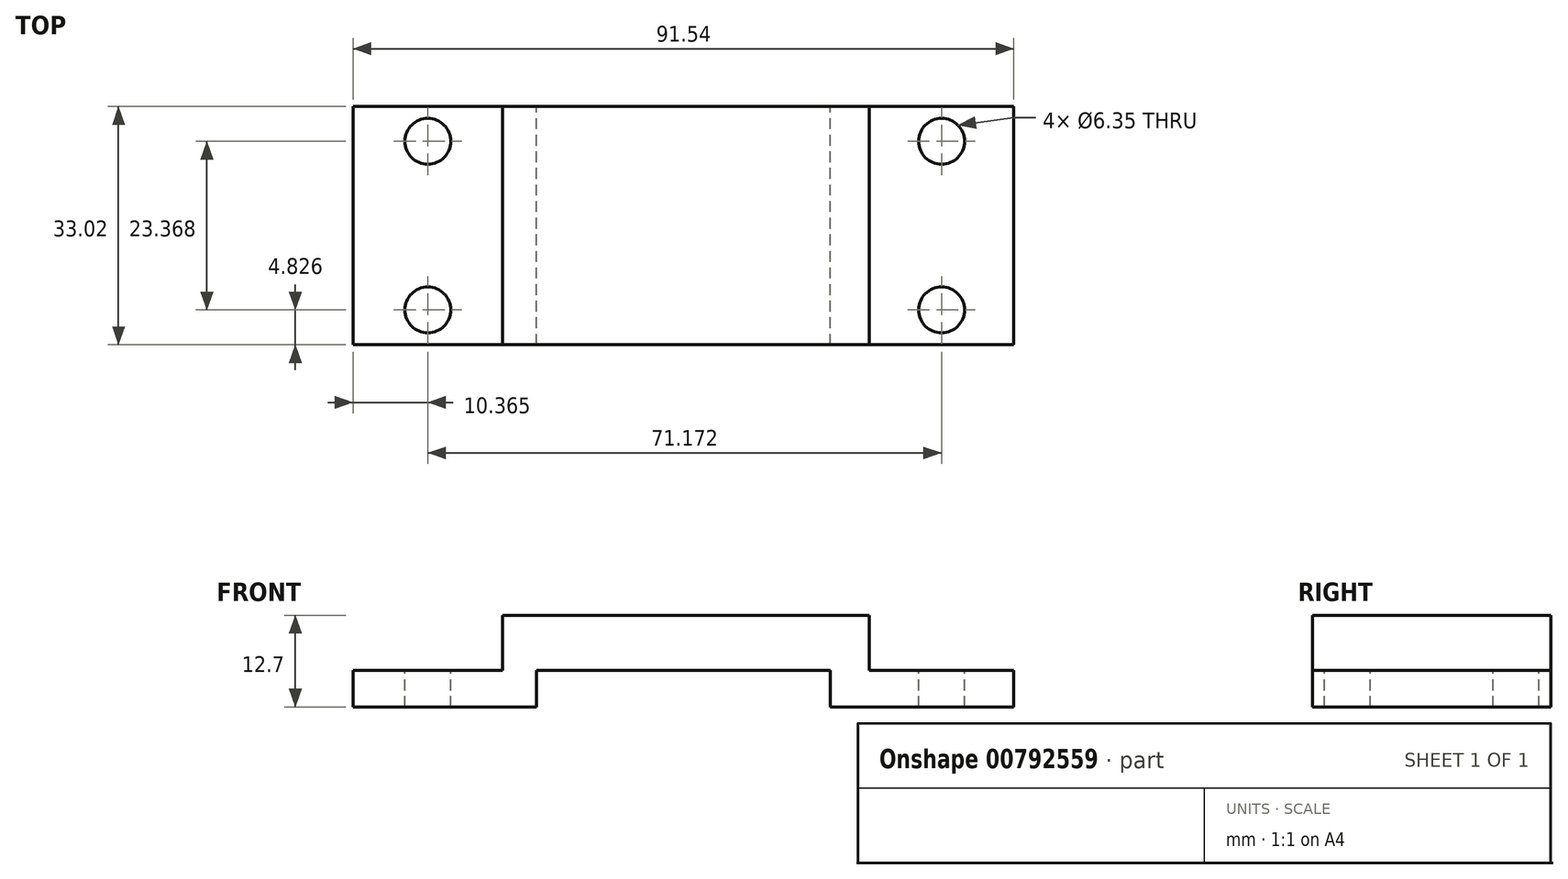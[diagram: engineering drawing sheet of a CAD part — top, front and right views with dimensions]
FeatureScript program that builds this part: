
annotation { "Feature Type Name" : "Feature", "Feature Type Description" : "" }
export const myFeature = defineFeature(function(context is Context, id is Id, definition is map)
    precondition{}
    {
        {
            var Q0;
            Q0=qCreatedBy(makeId("Front.planeOp"),FACE);
            var sketch = newSketch(context, id + "F0", { "sketchPlane" : qUnion([Q0])});
            skLineSegment(sketch, "E0.bottom", {"start": v(-20.64, 9.88) * mm, "end": v(30.16, 9.88) * mm});
            skLineSegment(sketch, "E0.top", {"start": v(-15.97, 2.26) * mm, "end": v(24.77, 2.26) * mm});
            skLineSegment(sketch, "E0.left", {"start": v(-20.64, 9.88) * mm, "end": v(-20.64, 2.26) * mm});
            skLineSegment(sketch, "E0.right", {"start": v(30.16, 9.88) * mm, "end": v(30.16, 2.26) * mm});
            skLineSegment(sketch, "E1.bottom", {"start": v(30.16, 2.26) * mm, "end": v(50.17, 2.26) * mm});
            skLineSegment(sketch, "E1.top", {"start": v(24.77, -2.82) * mm, "end": v(50.17, -2.82) * mm});
            skLineSegment(sketch, "E1.left", {"start": v(24.77, 2.26) * mm, "end": v(24.77, -2.82) * mm});
            skLineSegment(sketch, "E1.right", {"start": v(50.17, 2.26) * mm, "end": v(50.17, -2.82) * mm});
            skLineSegment(sketch, "E2.bottom", {"start": v(-20.64, 2.26) * mm, "end": v(-41.37, 2.26) * mm});
            skLineSegment(sketch, "E2.top", {"start": v(-15.97, -2.82) * mm, "end": v(-41.37, -2.82) * mm});
            skLineSegment(sketch, "E2.left", {"start": v(-15.97, 2.26) * mm, "end": v(-15.97, -2.82) * mm});
            skLineSegment(sketch, "E2.right", {"start": v(-41.37, 2.26) * mm, "end": v(-41.37, -2.82) * mm});
            skSolve(sketch);
        }
        {
            var Q0;
            Q0=makeQuery(id+"F0.imprint","IMPRINT",FACE,{"disambiguationData":[TD([[makeQuery(id+"F0.imprint","IMPRINT",EDGE,{"derivedFrom":sQuery(id+"F0.wireOp",EDGE,"E0.bottom")}),-1.0]])]});
            extrude(context, id + "F1", {"entities" : qUnion([Q0]), "depth" : 33.02 * mm, "offsetDistance" : 25.4 * mm});
        }
        {
            var Q0;
            Q0=makeQuery(id+"F1.opExtrude","SWEPT_FACE",FACE,{"disambiguationData":[OSD([sQuery(id+"F0.wireOp",EDGE,"E2.bottom")])]});
            var sketch = newSketch(context, id + "F2", { "sketchPlane" : qUnion([Q0])});
            skLineSegment(sketch, "E3", {"start": v(-41.37, -18.28) * mm, "end": v(-20.64, -18.28) * mm, "construction": true});
            skLineSegment(sketch, "E4", {"start": v(-31, -33.02) * mm, "end": v(-31, 0) * mm, "construction": true});
            skLineSegment(sketch, "E5", {"start": v(-37.64, 0) * mm, "end": v(-37.64, -4.83) * mm, "construction": true});
            skLineSegment(sketch, "E6", {"start": v(-37.64, -33.02) * mm, "end": v(-37.64, -28.2) * mm, "construction": true});
            skCircle(sketch, "E7", {"center": v(-31, -28.2) * mm, "radius": 3.18 * mm});
            skCircle(sketch, "E8", {"center": v(-31, -4.83) * mm, "radius": 3.18 * mm});
            skSolve(sketch);
        }
        {
            var Q0;
            Q0=makeQuery(id+"F2.imprint","IMPRINT",FACE,{"disambiguationData":[TD([[makeQuery(id+"F2.imprint","IMPRINT",EDGE,{"derivedFrom":sQuery(id+"F2.wireOp",EDGE,"E7")}),1.0]])]});
            var Q1;
            Q1=makeQuery(id+"F2.imprint","IMPRINT",FACE,{"disambiguationData":[TD([[makeQuery(id+"F2.imprint","IMPRINT",EDGE,{"derivedFrom":sQuery(id+"F2.wireOp",EDGE,"E8")}),1.0]])]});
            extrude(context, id + "F3", {"entities" : qUnion([Q0, Q1]), "operationType" : NewBodyOperationType.REMOVE, "oppositeDirection" : true, "depth" : 25.4 * mm, "offsetDistance" : 25.4 * mm});
        }
        {
            var Q0;
            Q0=makeQuery(id+"F1.opExtrude","SWEPT_FACE",FACE,{"disambiguationData":[OSD([sQuery(id+"F0.wireOp",EDGE,"E1.bottom")])]});
            var sketch = newSketch(context, id + "F4", { "sketchPlane" : qUnion([Q0])});
            skLineSegment(sketch, "E9", {"start": v(30.16, -16.51) * mm, "end": v(50.17, -16.51) * mm, "construction": true});
            skLineSegment(sketch, "E10", {"start": v(40.17, -33.02) * mm, "end": v(40.17, 0) * mm, "construction": true});
            skLineSegment(sketch, "E11", {"start": v(46.68, 0) * mm, "end": v(46.68, -4.83) * mm, "construction": true});
            skLineSegment(sketch, "E12", {"start": v(46.46, -33.02) * mm, "end": v(46.46, -28.2) * mm, "construction": true});
            skCircle(sketch, "E13", {"center": v(40.17, -4.83) * mm, "radius": 3.18 * mm});
            skCircle(sketch, "E14", {"center": v(40.17, -28.2) * mm, "radius": 3.18 * mm});
            skSolve(sketch);
        }
        {
            var Q0;
            Q0=makeQuery(id+"F4.imprint","IMPRINT",FACE,{"disambiguationData":[TD([[makeQuery(id+"F4.imprint","IMPRINT",EDGE,{"derivedFrom":sQuery(id+"F4.wireOp",EDGE,"E13")}),1.0]])]});
            var Q1;
            Q1=makeQuery(id+"F4.imprint","IMPRINT",FACE,{"disambiguationData":[TD([[makeQuery(id+"F4.imprint","IMPRINT",EDGE,{"derivedFrom":sQuery(id+"F4.wireOp",EDGE,"E14")}),1.0]])]});
            extrude(context, id + "F5", {"entities" : qUnion([Q0, Q1]), "operationType" : NewBodyOperationType.REMOVE, "oppositeDirection" : true, "depth" : 25.4 * mm, "offsetDistance" : 25.4 * mm});
        }
    });
